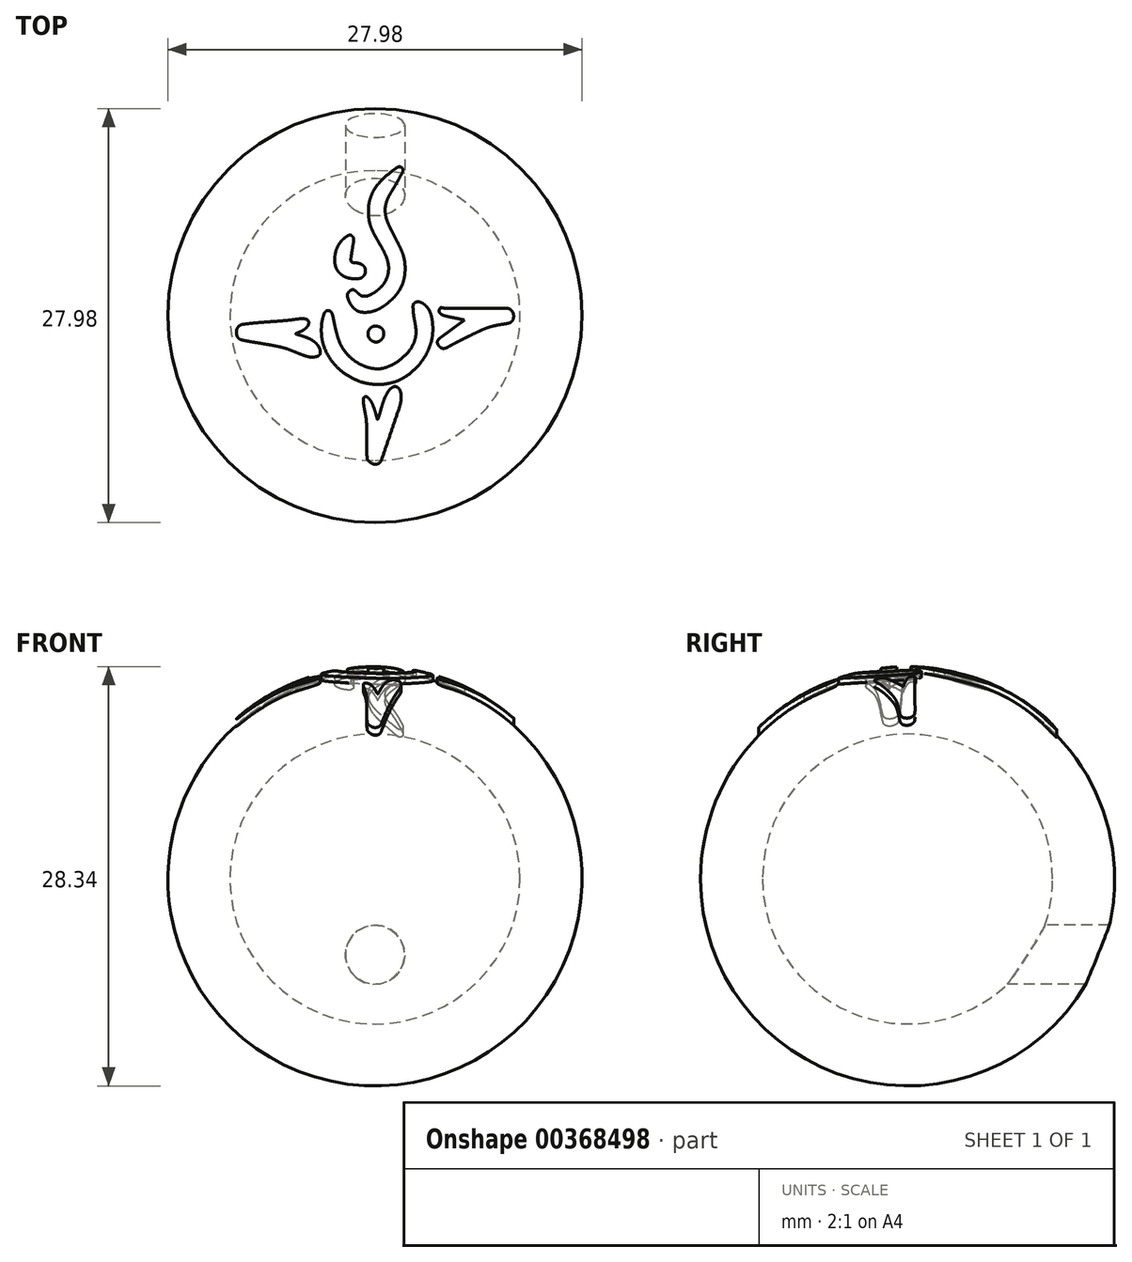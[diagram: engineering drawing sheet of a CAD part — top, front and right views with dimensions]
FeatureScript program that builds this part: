
annotation { "Feature Type Name" : "Feature", "Feature Type Description" : "" }
export const myFeature = defineFeature(function(context is Context, id is Id, definition is map)
    precondition{}
    {
        {
            var Q0;
            Q0=qCreatedBy(makeId("Top.planeOp"),FACE);
            var sketch = newSketch(context, id + "F0", { "sketchPlane" : qUnion([Q0])});
            skLineSegment(sketch, "E0", {"start": v(0, -10) * mm, "end": v(0, 10) * mm});
            skArc(sketch, "E1", {"start": v(0, 10) * mm, "mid": v(-10, 0) * mm, "end": v(0, -10) * mm});
            skSolve(sketch);
        }
        {
            var Q0;
            {var subQ0=sQuery(id+"F0.wireOp",EDGE,"E1");Q0=makeQuery(id+"F0.imprint","IMPRINT",FACE,{"disambiguationData":[TD([[makeQuery(id+"F0.imprint","IMPRINT",EDGE,{"derivedFrom":subQ0}),1.0]])]});}
            var Q1;
            Q1=sQuery(id+"F0.wireOp",EDGE,"E0");
            revolve(context, id + "F1", {"entities" : qUnion([Q0]), "axis" : qUnion([Q1]), "revolveType" : RevolveType.FULL});
        }
        {
            var Q0;
            Q0=makeQuery(id+"F1.opRevolve","SWEPT_BODY",BODY,{"disambiguationData":[OSD([sQuery(id+"F0.wireOp",EDGE,"E0"),sQuery(id+"F0.wireOp",EDGE,"E1")])]});
            var Q1;
            Q1=sQuery(id+"F0.wireOp",VERTEX,"NPe4G0ez-t7S9-9isL-QO5v-uuJu600mHcIT.center");
            var Q2;
            Q2=sQuery(id+"F0.wireOp",VERTEX,"E1.center");
            transform(context, id + "F2", {"entities" : qUnion([Q0]), "transformType" : TransformType.SCALE_UNIFORMLY, "scale" : 33.3, "scalePoint" : qUnion([Q2]), "makeCopy" : false});
        }
        {
            var Q0;
            Q0=qCreatedBy(makeId("Top.planeOp"),FACE);
            var sketch = newSketch(context, id + "F3", { "sketchPlane" : qUnion([Q0])});
            skArc(sketch, "E2", {"start": v(29.01, 233.55) * mm, "mid": v(19.13, 225.53) * mm, "end": v(9.84, 216.83) * mm});
            skArc(sketch, "E3", {"start": v(9.84, 216.83) * mm, "mid": v(3.12, 209.1) * mm, "end": v(-2.51, 200.54) * mm});
            skArc(sketch, "E4", {"start": v(-2.51, 200.54) * mm, "mid": v(-6.44, 192.13) * mm, "end": v(-9.04, 183.21) * mm});
            skArc(sketch, "E5", {"start": v(-9.04, 183.21) * mm, "mid": v(-10.44, 173.41) * mm, "end": v(-10.58, 163.51) * mm});
            skArc(sketch, "E6", {"start": v(-10.58, 163.51) * mm, "mid": v(-10.1, 157.75) * mm, "end": v(-9.24, 152.03) * mm});
            skArc(sketch, "E7", {"start": v(-9.24, 152.03) * mm, "mid": v(-8.07, 147.04) * mm, "end": v(-6.42, 142.18) * mm});
            skArc(sketch, "E8", {"start": v(-6.42, 142.18) * mm, "mid": v(-3.83, 136.15) * mm, "end": v(-0.88, 130.3) * mm});
            skArc(sketch, "E9", {"start": v(-0.88, 130.3) * mm, "mid": v(4.67, 120.25) * mm, "end": v(10.35, 110.28) * mm});
            skArc(sketch, "E10", {"start": v(10.35, 110.28) * mm, "mid": v(14.5, 102.5) * mm, "end": v(18.1, 94.45) * mm});
            skArc(sketch, "E11", {"start": v(18.1, 94.45) * mm, "mid": v(20.33, 87.78) * mm, "end": v(21.65, 80.87) * mm});
            skArc(sketch, "E12", {"start": v(21.65, 80.87) * mm, "mid": v(21.93, 74.62) * mm, "end": v(21.23, 68.4) * mm});
            skArc(sketch, "E13", {"start": v(21.23, 68.4) * mm, "mid": v(19.56, 62.07) * mm, "end": v(17.04, 56.03) * mm});
            skArc(sketch, "E14", {"start": v(17.04, 56.03) * mm, "mid": v(14.27, 51.34) * mm, "end": v(10.87, 47.1) * mm});
            skArc(sketch, "E15", {"start": v(10.87, 47.1) * mm, "mid": v(6.45, 42.75) * mm, "end": v(1.63, 38.84) * mm});
            skArc(sketch, "E16", {"start": v(1.63, 38.84) * mm, "mid": v(-3.27, 35.59) * mm, "end": v(-8.46, 32.84) * mm});
            skArc(sketch, "E17", {"start": v(-8.46, 32.84) * mm, "mid": v(-12.69, 31.4) * mm, "end": v(-17.12, 30.9) * mm});
            skArc(sketch, "E18", {"start": v(-17.12, 30.9) * mm, "mid": v(-18.57, 30.96) * mm, "end": v(-20.02, 31.11) * mm});
            skArc(sketch, "E19", {"start": v(-20.02, 31.11) * mm, "mid": v(-21.08, 31.35) * mm, "end": v(-22.08, 31.77) * mm});
            skArc(sketch, "E20", {"start": v(-22.08, 31.77) * mm, "mid": v(-23.2, 32.43) * mm, "end": v(-24.25, 33.22) * mm});
            skArc(sketch, "E21", {"start": v(-24.25, 33.22) * mm, "mid": v(-26.12, 34.84) * mm, "end": v(-27.96, 36.5) * mm});
            skArc(sketch, "E22", {"start": v(-27.96, 36.5) * mm, "mid": v(-29.65, 38.02) * mm, "end": v(-31.37, 39.52) * mm});
            skArc(sketch, "E23", {"start": v(-31.37, 39.52) * mm, "mid": v(-32.36, 40.29) * mm, "end": v(-33.42, 40.95) * mm});
            skArc(sketch, "E24", {"start": v(-33.42, 40.95) * mm, "mid": v(-34.2, 41.3) * mm, "end": v(-35.03, 41.5) * mm});
            skArc(sketch, "E25", {"start": v(-35.03, 41.5) * mm, "mid": v(-35.87, 41.54) * mm, "end": v(-36.7, 41.42) * mm});
            skArc(sketch, "E26", {"start": v(-36.7, 41.42) * mm, "mid": v(-38, 41) * mm, "end": v(-39.22, 40.4) * mm});
            skArc(sketch, "E27", {"start": v(-39.22, 40.4) * mm, "mid": v(-40.42, 39.6) * mm, "end": v(-41.52, 38.67) * mm});
            skArc(sketch, "E28", {"start": v(-41.52, 38.67) * mm, "mid": v(-42.45, 37.64) * mm, "end": v(-43.25, 36.51) * mm});
            skArc(sketch, "E29", {"start": v(-43.25, 36.51) * mm, "mid": v(-43.8, 35.42) * mm, "end": v(-44.14, 34.24) * mm});
            skArc(sketch, "E30", {"start": v(-44.14, 34.24) * mm, "mid": v(-44.33, 31.9) * mm, "end": v(-44.03, 29.59) * mm});
            skArc(sketch, "E31", {"start": v(-44.03, 29.59) * mm, "mid": v(-43.16, 26.53) * mm, "end": v(-42.02, 23.57) * mm});
            skArc(sketch, "E32", {"start": v(-42.02, 23.57) * mm, "mid": v(-40.5, 20.42) * mm, "end": v(-38.71, 17.4) * mm});
            skArc(sketch, "E33", {"start": v(-38.71, 17.4) * mm, "mid": v(-36.76, 14.69) * mm, "end": v(-34.56, 12.17) * mm});
            skArc(sketch, "E34", {"start": v(-34.56, 12.17) * mm, "mid": v(-32.5, 10.26) * mm, "end": v(-30.24, 8.58) * mm});
            skArc(sketch, "E35", {"start": v(-30.24, 8.58) * mm, "mid": v(-27.94, 7.28) * mm, "end": v(-25.49, 6.3) * mm});
            skArc(sketch, "E36", {"start": v(-25.49, 6.3) * mm, "mid": v(-22.72, 5.57) * mm, "end": v(-19.9, 5.18) * mm});
            skArc(sketch, "E37", {"start": v(-19.9, 5.18) * mm, "mid": v(-16.44, 5.03) * mm, "end": v(-12.99, 5.12) * mm});
            skArc(sketch, "E38", {"start": v(-12.99, 5.12) * mm, "mid": v(-7.73, 5.76) * mm, "end": v(-2.58, 7.01) * mm});
            skArc(sketch, "E39", {"start": v(-2.58, 7.01) * mm, "mid": v(2.77, 8.95) * mm, "end": v(7.9, 11.39) * mm});
            skArc(sketch, "E40", {"start": v(7.9, 11.39) * mm, "mid": v(13.3, 14.6) * mm, "end": v(18.4, 18.25) * mm});
            skArc(sketch, "E41", {"start": v(18.4, 18.25) * mm, "mid": v(23.75, 22.74) * mm, "end": v(28.83, 27.56) * mm});
            skArc(sketch, "E42", {"start": v(28.83, 27.56) * mm, "mid": v(33.48, 32.7) * mm, "end": v(37.66, 38.24) * mm});
            skArc(sketch, "E43", {"start": v(37.66, 38.24) * mm, "mid": v(41.04, 43.77) * mm, "end": v(43.8, 49.62) * mm});
            skArc(sketch, "E44", {"start": v(43.8, 49.62) * mm, "mid": v(45.9, 55.75) * mm, "end": v(47.34, 62.07) * mm});
            skArc(sketch, "E45", {"start": v(47.34, 62.07) * mm, "mid": v(48.2, 68.96) * mm, "end": v(48.46, 75.9) * mm});
            skArc(sketch, "E46", {"start": v(48.46, 75.9) * mm, "mid": v(48.28, 80.88) * mm, "end": v(47.83, 85.83) * mm});
            skArc(sketch, "E47", {"start": v(47.83, 85.83) * mm, "mid": v(47.14, 90.3) * mm, "end": v(46.11, 94.69) * mm});
            skArc(sketch, "E48", {"start": v(46.11, 94.69) * mm, "mid": v(44.7, 99.28) * mm, "end": v(42.96, 103.76) * mm});
            skArc(sketch, "E49", {"start": v(42.96, 103.76) * mm, "mid": v(40.56, 109.13) * mm, "end": v(37.96, 114.4) * mm});
            skArc(sketch, "E50", {"start": v(37.96, 114.4) * mm, "mid": v(32.65, 124.74) * mm, "end": v(27.37, 135.1) * mm});
            skArc(sketch, "E51", {"start": v(27.37, 135.1) * mm, "mid": v(24.73, 140.42) * mm, "end": v(22.2, 145.8) * mm});
            skArc(sketch, "E52", {"start": v(22.2, 145.8) * mm, "mid": v(20.66, 149.32) * mm, "end": v(19.27, 152.9) * mm});
            skArc(sketch, "E53", {"start": v(19.27, 152.9) * mm, "mid": v(18.3, 155.87) * mm, "end": v(17.54, 158.9) * mm});
            skArc(sketch, "E54", {"start": v(17.54, 158.9) * mm, "mid": v(16.72, 163.9) * mm, "end": v(16.36, 168.93) * mm});
            skArc(sketch, "E55", {"start": v(16.36, 168.93) * mm, "mid": v(16.52, 173.6) * mm, "end": v(17.22, 178.24) * mm});
            skArc(sketch, "E56", {"start": v(17.22, 178.24) * mm, "mid": v(18.5, 183.02) * mm, "end": v(20.27, 187.63) * mm});
            skArc(sketch, "E57", {"start": v(20.27, 187.63) * mm, "mid": v(22.83, 192.87) * mm, "end": v(25.73, 197.93) * mm});
            skArc(sketch, "E58", {"start": v(25.73, 197.93) * mm, "mid": v(28.95, 203.25) * mm, "end": v(32.1, 208.61) * mm});
            skArc(sketch, "E59", {"start": v(32.1, 208.61) * mm, "mid": v(35.38, 214.4) * mm, "end": v(38.59, 220.22) * mm});
            skArc(sketch, "E60", {"start": v(38.59, 220.22) * mm, "mid": v(41.58, 225.77) * mm, "end": v(44.55, 231.33) * mm});
            skArc(sketch, "E61", {"start": v(44.55, 231.33) * mm, "mid": v(45, 232.47) * mm, "end": v(45.14, 233.69) * mm});
            skArc(sketch, "E62", {"start": v(45.14, 233.69) * mm, "mid": v(45.05, 234.64) * mm, "end": v(44.77, 235.56) * mm});
            skArc(sketch, "E63", {"start": v(44.77, 235.56) * mm, "mid": v(44.32, 236.46) * mm, "end": v(43.72, 237.27) * mm});
            skArc(sketch, "E64", {"start": v(43.72, 237.27) * mm, "mid": v(42.97, 238) * mm, "end": v(42.1, 238.6) * mm});
            skArc(sketch, "E65", {"start": v(42.1, 238.6) * mm, "mid": v(41.14, 239.08) * mm, "end": v(40.11, 239.4) * mm});
            skArc(sketch, "E66", {"start": v(40.11, 239.4) * mm, "mid": v(39.26, 239.5) * mm, "end": v(38.42, 239.4) * mm});
            skArc(sketch, "E67", {"start": v(38.42, 239.4) * mm, "mid": v(37.38, 239.07) * mm, "end": v(36.4, 238.62) * mm});
            skArc(sketch, "E68", {"start": v(36.4, 238.62) * mm, "mid": v(34.96, 237.8) * mm, "end": v(33.58, 236.9) * mm});
            skArc(sketch, "E69", {"start": v(33.58, 236.9) * mm, "mid": v(31.29, 235.24) * mm, "end": v(29.01, 233.55) * mm});
            skArc(sketch, "E70", {"start": v(-45.92, 127.08) * mm, "mid": v(-50.13, 123.98) * mm, "end": v(-53.86, 120.31) * mm});
            skArc(sketch, "E71", {"start": v(-53.86, 120.31) * mm, "mid": v(-57.15, 116.09) * mm, "end": v(-59.87, 111.47) * mm});
            skArc(sketch, "E72", {"start": v(-59.87, 111.47) * mm, "mid": v(-62.06, 106.35) * mm, "end": v(-63.6, 101) * mm});
            skArc(sketch, "E73", {"start": v(-63.6, 101) * mm, "mid": v(-64.54, 95.27) * mm, "end": v(-64.85, 89.48) * mm});
            skArc(sketch, "E74", {"start": v(-64.85, 89.48) * mm, "mid": v(-64.72, 86.13) * mm, "end": v(-64.34, 82.8) * mm});
            skArc(sketch, "E75", {"start": v(-64.34, 82.8) * mm, "mid": v(-63.74, 79.95) * mm, "end": v(-62.82, 77.18) * mm});
            skArc(sketch, "E76", {"start": v(-62.82, 77.18) * mm, "mid": v(-61.64, 74.64) * mm, "end": v(-60.16, 72.26) * mm});
            skArc(sketch, "E77", {"start": v(-60.16, 72.26) * mm, "mid": v(-58.3, 69.89) * mm, "end": v(-56.23, 67.7) * mm});
            skArc(sketch, "E78", {"start": v(-56.23, 67.7) * mm, "mid": v(-54.01, 65.77) * mm, "end": v(-51.62, 64.06) * mm});
            skArc(sketch, "E79", {"start": v(-51.62, 64.06) * mm, "mid": v(-49.17, 62.64) * mm, "end": v(-46.6, 61.5) * mm});
            skArc(sketch, "E80", {"start": v(-46.6, 61.5) * mm, "mid": v(-43.73, 60.56) * mm, "end": v(-40.8, 59.9) * mm});
            skArc(sketch, "E81", {"start": v(-40.8, 59.9) * mm, "mid": v(-37.34, 59.42) * mm, "end": v(-33.86, 59.16) * mm});
            skArc(sketch, "E82", {"start": v(-33.86, 59.16) * mm, "mid": v(-30.5, 59.1) * mm, "end": v(-27.13, 59.26) * mm});
            skArc(sketch, "E83", {"start": v(-27.13, 59.26) * mm, "mid": v(-24.75, 59.62) * mm, "end": v(-22.46, 60.36) * mm});
            skArc(sketch, "E84", {"start": v(-22.46, 60.36) * mm, "mid": v(-20.66, 61.32) * mm, "end": v(-19.1, 62.63) * mm});
            skArc(sketch, "E85", {"start": v(-19.1, 62.63) * mm, "mid": v(-17.66, 64.36) * mm, "end": v(-16.5, 66.28) * mm});
            skArc(sketch, "E86", {"start": v(-16.5, 66.28) * mm, "mid": v(-15.4, 69.6) * mm, "end": v(-15.24, 73.08) * mm});
            skArc(sketch, "E87", {"start": v(-15.24, 73.08) * mm, "mid": v(-16.08, 76.33) * mm, "end": v(-17.88, 79.16) * mm});
            skArc(sketch, "E88", {"start": v(-17.88, 79.16) * mm, "mid": v(-20.75, 81.68) * mm, "end": v(-24.17, 83.38) * mm});
            skArc(sketch, "E89", {"start": v(-24.17, 83.38) * mm, "mid": v(-28.48, 84.49) * mm, "end": v(-32.91, 84.88) * mm});
            skArc(sketch, "E90", {"start": v(-32.91, 84.88) * mm, "mid": v(-34.86, 85.1) * mm, "end": v(-36.73, 85.7) * mm});
            skArc(sketch, "E91", {"start": v(-36.73, 85.7) * mm, "mid": v(-37.9, 86.6) * mm, "end": v(-38.52, 87.91) * mm});
            skArc(sketch, "E92", {"start": v(-38.52, 87.91) * mm, "mid": v(-38.8, 90.23) * mm, "end": v(-38.7, 92.56) * mm});
            skArc(sketch, "E93", {"start": v(-38.7, 92.56) * mm, "mid": v(-37.86, 98.3) * mm, "end": v(-36.95, 104.03) * mm});
            skArc(sketch, "E94", {"start": v(-36.95, 104.03) * mm, "mid": v(-35.78, 111.04) * mm, "end": v(-34.64, 118.06) * mm});
            skArc(sketch, "E95", {"start": v(-34.64, 118.06) * mm, "mid": v(-34.36, 120.3) * mm, "end": v(-34.22, 122.54) * mm});
            skArc(sketch, "E96", {"start": v(-34.22, 122.54) * mm, "mid": v(-34.32, 123.85) * mm, "end": v(-34.7, 125.11) * mm});
            skArc(sketch, "E97", {"start": v(-34.7, 125.11) * mm, "mid": v(-35.37, 126.33) * mm, "end": v(-36.26, 127.4) * mm});
            skArc(sketch, "E98", {"start": v(-36.26, 127.4) * mm, "mid": v(-37.31, 128.36) * mm, "end": v(-38.46, 129.21) * mm});
            skArc(sketch, "E99", {"start": v(-38.46, 129.21) * mm, "mid": v(-39.3, 129.61) * mm, "end": v(-40.24, 129.73) * mm});
            skArc(sketch, "E100", {"start": v(-40.24, 129.73) * mm, "mid": v(-41.31, 129.57) * mm, "end": v(-42.32, 129.17) * mm});
            skArc(sketch, "E101", {"start": v(-42.32, 129.17) * mm, "mid": v(-44.14, 128.16) * mm, "end": v(-45.92, 127.08) * mm});
            skArc(sketch, "E102", {"start": v(65.46, 21.4) * mm, "mid": v(64.85, 21.12) * mm, "end": v(64.26, 20.79) * mm});
            skArc(sketch, "E103", {"start": v(64.26, 20.79) * mm, "mid": v(63.68, 20.42) * mm, "end": v(63.13, 20) * mm});
            skArc(sketch, "E104", {"start": v(63.13, 20) * mm, "mid": v(62.68, 19.6) * mm, "end": v(62.25, 19.18) * mm});
            skArc(sketch, "E105", {"start": v(62.25, 19.18) * mm, "mid": v(61.98, 18.83) * mm, "end": v(61.79, 18.44) * mm});
            skArc(sketch, "E106", {"start": v(61.79, 18.44) * mm, "mid": v(61.29, 16.67) * mm, "end": v(61.1, 14.84) * mm});
            skArc(sketch, "E107", {"start": v(61.1, 14.84) * mm, "mid": v(61.15, 11.63) * mm, "end": v(61.3, 8.43) * mm});
            skArc(sketch, "E108", {"start": v(61.3, 8.43) * mm, "mid": v(61.65, 4.5) * mm, "end": v(62.14, 0.6) * mm});
            skArc(sketch, "E109", {"start": v(62.14, 0.6) * mm, "mid": v(62.82, -3.76) * mm, "end": v(63.62, -8.1) * mm});
            skArc(sketch, "E110", {"start": v(63.62, -8.1) * mm, "mid": v(64.53, -12.99) * mm, "end": v(65.32, -17.9) * mm});
            skArc(sketch, "E111", {"start": v(65.32, -17.9) * mm, "mid": v(65.76, -21.56) * mm, "end": v(65.99, -25.23) * mm});
            skArc(sketch, "E112", {"start": v(65.99, -25.23) * mm, "mid": v(65.98, -28.33) * mm, "end": v(65.74, -31.42) * mm});
            skArc(sketch, "E113", {"start": v(65.74, -31.42) * mm, "mid": v(65.29, -34.5) * mm, "end": v(64.6, -37.55) * mm});
            skArc(sketch, "E114", {"start": v(64.6, -37.55) * mm, "mid": v(61.01, -47.26) * mm, "end": v(55.57, -56.05) * mm});
            skArc(sketch, "E115", {"start": v(55.57, -56.05) * mm, "mid": v(47.83, -64.8) * mm, "end": v(38.95, -72.38) * mm});
            skArc(sketch, "E116", {"start": v(38.95, -72.38) * mm, "mid": v(29.3, -78.52) * mm, "end": v(18.86, -83.23) * mm});
            skArc(sketch, "E117", {"start": v(18.86, -83.23) * mm, "mid": v(9.39, -85.53) * mm, "end": v(-0.36, -85.64) * mm});
            skArc(sketch, "E118", {"start": v(-0.36, -85.64) * mm, "mid": v(-9.01, -84.12) * mm, "end": v(-17.37, -81.43) * mm});
            skArc(sketch, "E119", {"start": v(-17.37, -81.43) * mm, "mid": v(-25.6, -77.52) * mm, "end": v(-33.3, -72.63) * mm});
            skArc(sketch, "E120", {"start": v(-33.3, -72.63) * mm, "mid": v(-40.35, -66.8) * mm, "end": v(-46.63, -60.13) * mm});
            skArc(sketch, "E121", {"start": v(-46.63, -60.13) * mm, "mid": v(-51.86, -52.93) * mm, "end": v(-56.07, -45.1) * mm});
            skArc(sketch, "E122", {"start": v(-56.07, -45.1) * mm, "mid": v(-57.45, -41.85) * mm, "end": v(-58.65, -38.55) * mm});
            skArc(sketch, "E123", {"start": v(-58.65, -38.55) * mm, "mid": v(-59.98, -34.42) * mm, "end": v(-61.19, -30.25) * mm});
            skArc(sketch, "E124", {"start": v(-61.19, -30.25) * mm, "mid": v(-62.51, -25.22) * mm, "end": v(-63.72, -20.17) * mm});
            skArc(sketch, "E125", {"start": v(-63.72, -20.17) * mm, "mid": v(-65.05, -14.14) * mm, "end": v(-66.29, -8.1) * mm});
            skArc(sketch, "E126", {"start": v(-66.29, -8.1) * mm, "mid": v(-67.21, -3.72) * mm, "end": v(-68.25, 0.62) * mm});
            skArc(sketch, "E127", {"start": v(-68.25, 0.62) * mm, "mid": v(-68.99, 2.87) * mm, "end": v(-70.04, 4.98) * mm});
            skArc(sketch, "E128", {"start": v(-70.04, 4.98) * mm, "mid": v(-71.06, 6.23) * mm, "end": v(-72.4, 7.13) * mm});
            skArc(sketch, "E129", {"start": v(-72.4, 7.13) * mm, "mid": v(-74.06, 7.7) * mm, "end": v(-75.82, 7.9) * mm});
            skArc(sketch, "E130", {"start": v(-75.82, 7.9) * mm, "mid": v(-77.16, 7.74) * mm, "end": v(-78.43, 7.27) * mm});
            skArc(sketch, "E131", {"start": v(-78.43, 7.27) * mm, "mid": v(-79.54, 6.5) * mm, "end": v(-80.43, 5.5) * mm});
            skArc(sketch, "E132", {"start": v(-80.43, 5.5) * mm, "mid": v(-81.4, 3.84) * mm, "end": v(-82.13, 2.07) * mm});
            skArc(sketch, "E133", {"start": v(-82.13, 2.07) * mm, "mid": v(-83.1, -1) * mm, "end": v(-83.99, -4.1) * mm});
            skArc(sketch, "E134", {"start": v(-83.99, -4.1) * mm, "mid": v(-85.1, -9.01) * mm, "end": v(-85.83, -14) * mm});
            skArc(sketch, "E135", {"start": v(-85.83, -14) * mm, "mid": v(-86.25, -19.46) * mm, "end": v(-86.34, -24.93) * mm});
            skArc(sketch, "E136", {"start": v(-86.34, -24.93) * mm, "mid": v(-86.1, -30.38) * mm, "end": v(-85.54, -35.8) * mm});
            skArc(sketch, "E137", {"start": v(-85.54, -35.8) * mm, "mid": v(-84.67, -40.74) * mm, "end": v(-83.43, -45.6) * mm});
            skArc(sketch, "E138", {"start": v(-83.43, -45.6) * mm, "mid": v(-77.13, -61.14) * mm, "end": v(-68, -75.2) * mm});
            skArc(sketch, "E139", {"start": v(-68, -75.2) * mm, "mid": v(-56.22, -87.58) * mm, "end": v(-42.42, -97.64) * mm});
            skArc(sketch, "E140", {"start": v(-42.42, -97.64) * mm, "mid": v(-27.05, -105.06) * mm, "end": v(-10.6, -109.6) * mm});
            skArc(sketch, "E141", {"start": v(-10.6, -109.6) * mm, "mid": v(6.07, -111) * mm, "end": v(22.7, -109.2) * mm});
            skArc(sketch, "E142", {"start": v(22.7, -109.2) * mm, "mid": v(34.18, -105.87) * mm, "end": v(45, -100.8) * mm});
            skArc(sketch, "E143", {"start": v(45, -100.8) * mm, "mid": v(55.53, -93.83) * mm, "end": v(65.05, -85.53) * mm});
            skArc(sketch, "E144", {"start": v(65.05, -85.53) * mm, "mid": v(73.6, -75.81) * mm, "end": v(80.84, -65.07) * mm});
            skArc(sketch, "E145", {"start": v(80.84, -65.07) * mm, "mid": v(86.55, -53.59) * mm, "end": v(90.67, -41.45) * mm});
            skArc(sketch, "E146", {"start": v(90.67, -41.45) * mm, "mid": v(91.87, -36) * mm, "end": v(92.6, -30.49) * mm});
            skArc(sketch, "E147", {"start": v(92.6, -30.49) * mm, "mid": v(92.96, -24.25) * mm, "end": v(92.94, -18) * mm});
            skArc(sketch, "E148", {"start": v(92.94, -18) * mm, "mid": v(92.53, -11.87) * mm, "end": v(91.75, -5.78) * mm});
            skArc(sketch, "E149", {"start": v(91.75, -5.78) * mm, "mid": v(90.67, -0.67) * mm, "end": v(89.09, 4.31) * mm});
            skArc(sketch, "E150", {"start": v(89.09, 4.31) * mm, "mid": v(87.2, 8.44) * mm, "end": v(84.75, 12.25) * mm});
            skArc(sketch, "E151", {"start": v(84.75, 12.25) * mm, "mid": v(81.83, 15.6) * mm, "end": v(78.44, 18.46) * mm});
            skArc(sketch, "E152", {"start": v(78.44, 18.46) * mm, "mid": v(75.14, 20.43) * mm, "end": v(71.54, 21.78) * mm});
            skArc(sketch, "E153", {"start": v(71.54, 21.78) * mm, "mid": v(68.47, 22.1) * mm, "end": v(65.46, 21.4) * mm});
            skArc(sketch, "E154", {"start": v(103.85, 10.27) * mm, "mid": v(103.2, 8.18) * mm, "end": v(103.3, 5.98) * mm});
            skArc(sketch, "E155", {"start": v(103.3, 5.98) * mm, "mid": v(104.13, 4.02) * mm, "end": v(105.62, 2.5) * mm});
            skArc(sketch, "E156", {"start": v(105.62, 2.5) * mm, "mid": v(108.58, 0.82) * mm, "end": v(111.77, -0.35) * mm});
            skArc(sketch, "E157", {"start": v(111.77, -0.35) * mm, "mid": v(117.43, -1.78) * mm, "end": v(123.14, -3) * mm});
            skArc(sketch, "E158", {"start": v(123.14, -3) * mm, "mid": v(125.34, -3.44) * mm, "end": v(127.55, -3.88) * mm});
            skArc(sketch, "E159", {"start": v(127.55, -3.88) * mm, "mid": v(129.83, -4.33) * mm, "end": v(132.11, -4.78) * mm});
            skArc(sketch, "E160", {"start": v(132.11, -4.78) * mm, "mid": v(134.16, -5.19) * mm, "end": v(136.2, -5.6) * mm});
            skArc(sketch, "E161", {"start": v(136.2, -5.6) * mm, "mid": v(137.57, -5.88) * mm, "end": v(138.94, -6.16) * mm});
            skLineSegment(sketch, "E162", {"start": v(138.94, -6.16) * mm, "end": v(144.24, -7.26) * mm});
            skLineSegment(sketch, "E163", {"start": v(144.24, -7.26) * mm, "end": v(138.6, -11.21) * mm});
            skArc(sketch, "E164", {"start": v(138.6, -11.21) * mm, "mid": v(137.18, -12.21) * mm, "end": v(135.77, -13.23) * mm});
            skArc(sketch, "E165", {"start": v(135.77, -13.23) * mm, "mid": v(133.77, -14.68) * mm, "end": v(131.77, -16.14) * mm});
            skArc(sketch, "E166", {"start": v(131.77, -16.14) * mm, "mid": v(129.58, -17.75) * mm, "end": v(127.4, -19.37) * mm});
            skArc(sketch, "E167", {"start": v(127.4, -19.37) * mm, "mid": v(125.35, -20.9) * mm, "end": v(123.3, -22.45) * mm});
            skArc(sketch, "E168", {"start": v(123.3, -22.45) * mm, "mid": v(121.22, -24) * mm, "end": v(119.15, -25.54) * mm});
            skArc(sketch, "E169", {"start": v(119.15, -25.54) * mm, "mid": v(116.91, -27.18) * mm, "end": v(114.67, -28.8) * mm});
            skArc(sketch, "E170", {"start": v(114.67, -28.8) * mm, "mid": v(112.6, -30.3) * mm, "end": v(110.53, -31.78) * mm});
            skArc(sketch, "E171", {"start": v(110.53, -31.78) * mm, "mid": v(109.02, -32.83) * mm, "end": v(107.5, -33.87) * mm});
            skArc(sketch, "E172", {"start": v(107.5, -33.87) * mm, "mid": v(104.91, -35.81) * mm, "end": v(102.52, -38) * mm});
            skArc(sketch, "E173", {"start": v(102.52, -38) * mm, "mid": v(101.18, -39.8) * mm, "end": v(100.4, -41.9) * mm});
            skArc(sketch, "E174", {"start": v(100.4, -41.9) * mm, "mid": v(100.3, -43.94) * mm, "end": v(100.88, -45.9) * mm});
            skArc(sketch, "E175", {"start": v(100.88, -45.9) * mm, "mid": v(102.25, -48.24) * mm, "end": v(103.94, -50.34) * mm});
            skArc(sketch, "E176", {"start": v(103.94, -50.34) * mm, "mid": v(105.3, -51.53) * mm, "end": v(106.85, -52.43) * mm});
            skArc(sketch, "E177", {"start": v(106.85, -52.43) * mm, "mid": v(108.5, -52.96) * mm, "end": v(110.22, -53.1) * mm});
            skArc(sketch, "E178", {"start": v(110.22, -53.1) * mm, "mid": v(112.2, -52.89) * mm, "end": v(114.12, -52.31) * mm});
            skArc(sketch, "E179", {"start": v(114.12, -52.31) * mm, "mid": v(116.4, -51.27) * mm, "end": v(118.59, -50.02) * mm});
            skArc(sketch, "E180", {"start": v(118.59, -50.02) * mm, "mid": v(120.15, -49.08) * mm, "end": v(121.76, -48.19) * mm});
            skArc(sketch, "E181", {"start": v(121.76, -48.19) * mm, "mid": v(125.82, -46.06) * mm, "end": v(129.89, -43.95) * mm});
            skArc(sketch, "E182", {"start": v(129.89, -43.95) * mm, "mid": v(134.76, -41.44) * mm, "end": v(139.64, -38.96) * mm});
            skArc(sketch, "E183", {"start": v(139.64, -38.96) * mm, "mid": v(144.95, -36.29) * mm, "end": v(150.27, -33.64) * mm});
            skArc(sketch, "E184", {"start": v(150.27, -33.64) * mm, "mid": v(159.77, -29) * mm, "end": v(169.33, -24.46) * mm});
            skArc(sketch, "E185", {"start": v(169.33, -24.46) * mm, "mid": v(175.2, -21.89) * mm, "end": v(181.2, -19.6) * mm});
            skArc(sketch, "E186", {"start": v(181.2, -19.6) * mm, "mid": v(186.48, -17.91) * mm, "end": v(191.84, -16.56) * mm});
            skArc(sketch, "E187", {"start": v(191.84, -16.56) * mm, "mid": v(198.67, -15.2) * mm, "end": v(205.54, -14.04) * mm});
            skArc(sketch, "E188", {"start": v(205.54, -14.04) * mm, "mid": v(208.79, -13.53) * mm, "end": v(212.03, -12.98) * mm});
            skArc(sketch, "E189", {"start": v(212.03, -12.98) * mm, "mid": v(213.87, -12.6) * mm, "end": v(215.7, -12.11) * mm});
            skArc(sketch, "E190", {"start": v(215.7, -12.11) * mm, "mid": v(216.92, -11.68) * mm, "end": v(218.09, -11.13) * mm});
            skArc(sketch, "E191", {"start": v(218.09, -11.13) * mm, "mid": v(219.06, -10.5) * mm, "end": v(219.93, -9.76) * mm});
            skArc(sketch, "E192", {"start": v(219.93, -9.76) * mm, "mid": v(221.11, -8.3) * mm, "end": v(221.97, -6.62) * mm});
            skArc(sketch, "E193", {"start": v(221.97, -6.62) * mm, "mid": v(222.6, -4.57) * mm, "end": v(222.93, -2.44) * mm});
            skArc(sketch, "E194", {"start": v(222.93, -2.44) * mm, "mid": v(222.96, -0.25) * mm, "end": v(222.7, 1.92) * mm});
            skArc(sketch, "E195", {"start": v(222.7, 1.92) * mm, "mid": v(222.14, 3.83) * mm, "end": v(221.24, 5.6) * mm});
            skArc(sketch, "E196", {"start": v(221.24, 5.6) * mm, "mid": v(219.73, 7.65) * mm, "end": v(217.92, 9.44) * mm});
            skArc(sketch, "E197", {"start": v(217.92, 9.44) * mm, "mid": v(216.13, 10.6) * mm, "end": v(214.1, 11.29) * mm});
            skArc(sketch, "E198", {"start": v(214.1, 11.29) * mm, "mid": v(210.86, 11.76) * mm, "end": v(207.59, 11.92) * mm});
            skArc(sketch, "E199", {"start": v(207.59, 11.92) * mm, "mid": v(198.73, 11.88) * mm, "end": v(189.88, 11.78) * mm});
            skArc(sketch, "E200", {"start": v(189.88, 11.78) * mm, "mid": v(175.63, 11.6) * mm, "end": v(161.38, 11.47) * mm});
            skArc(sketch, "E201", {"start": v(161.38, 11.47) * mm, "mid": v(148.64, 11.43) * mm, "end": v(135.9, 11.47) * mm});
            skArc(sketch, "E202", {"start": v(135.9, 11.47) * mm, "mid": v(125.01, 11.56) * mm, "end": v(114.12, 11.68) * mm});
            skArc(sketch, "E203", {"start": v(114.12, 11.68) * mm, "mid": v(111.53, 11.85) * mm, "end": v(108.98, 12.3) * mm});
            skArc(sketch, "E204", {"start": v(108.98, 12.3) * mm, "mid": v(107.88, 12.53) * mm, "end": v(106.78, 12.7) * mm});
            skArc(sketch, "E205", {"start": v(106.78, 12.7) * mm, "mid": v(106.2, 12.72) * mm, "end": v(105.65, 12.58) * mm});
            skArc(sketch, "E206", {"start": v(105.65, 12.58) * mm, "mid": v(105.18, 12.3) * mm, "end": v(104.81, 11.9) * mm});
            skArc(sketch, "E207", {"start": v(104.81, 11.9) * mm, "mid": v(104.3, 11.1) * mm, "end": v(103.85, 10.27) * mm});
            skArc(sketch, "E208", {"start": v(-131.36, -6.65) * mm, "mid": v(-133.6, -7) * mm, "end": v(-135.83, -7.27) * mm});
            skArc(sketch, "E209", {"start": v(-135.83, -7.27) * mm, "mid": v(-139.72, -7.68) * mm, "end": v(-143.62, -8.06) * mm});
            skArc(sketch, "E210", {"start": v(-143.62, -8.06) * mm, "mid": v(-148.14, -8.47) * mm, "end": v(-152.66, -8.86) * mm});
            skArc(sketch, "E211", {"start": v(-152.66, -8.86) * mm, "mid": v(-157.26, -9.22) * mm, "end": v(-161.86, -9.55) * mm});
            skArc(sketch, "E212", {"start": v(-161.86, -9.55) * mm, "mid": v(-173.2, -10.37) * mm, "end": v(-184.55, -11.25) * mm});
            skArc(sketch, "E213", {"start": v(-184.55, -11.25) * mm, "mid": v(-192.69, -11.96) * mm, "end": v(-200.81, -12.79) * mm});
            skArc(sketch, "E214", {"start": v(-200.81, -12.79) * mm, "mid": v(-206.72, -13.48) * mm, "end": v(-212.61, -14.24) * mm});
            skArc(sketch, "E215", {"start": v(-212.61, -14.24) * mm, "mid": v(-214.78, -14.73) * mm, "end": v(-216.83, -15.58) * mm});
            skArc(sketch, "E216", {"start": v(-216.83, -15.58) * mm, "mid": v(-219.48, -17.53) * mm, "end": v(-221.38, -20.22) * mm});
            skArc(sketch, "E217", {"start": v(-221.38, -20.22) * mm, "mid": v(-222.6, -23.66) * mm, "end": v(-222.98, -27.29) * mm});
            skArc(sketch, "E218", {"start": v(-222.98, -27.29) * mm, "mid": v(-222.51, -30.87) * mm, "end": v(-221.21, -34.25) * mm});
            skArc(sketch, "E219", {"start": v(-221.21, -34.25) * mm, "mid": v(-219.25, -36.82) * mm, "end": v(-216.57, -38.61) * mm});
            skArc(sketch, "E220", {"start": v(-216.57, -38.61) * mm, "mid": v(-215.48, -39.03) * mm, "end": v(-214.35, -39.34) * mm});
            skArc(sketch, "E221", {"start": v(-214.35, -39.34) * mm, "mid": v(-211.03, -40.03) * mm, "end": v(-207.7, -40.7) * mm});
            skArc(sketch, "E222", {"start": v(-207.7, -40.7) * mm, "mid": v(-203.7, -41.46) * mm, "end": v(-199.71, -42.18) * mm});
            skArc(sketch, "E223", {"start": v(-199.71, -42.18) * mm, "mid": v(-195.29, -42.94) * mm, "end": v(-190.86, -43.67) * mm});
            skArc(sketch, "E224", {"start": v(-190.86, -43.67) * mm, "mid": v(-179.98, -45.46) * mm, "end": v(-169.1, -47.31) * mm});
            skArc(sketch, "E225", {"start": v(-169.1, -47.31) * mm, "mid": v(-161.88, -48.66) * mm, "end": v(-154.68, -50.16) * mm});
            skArc(sketch, "E226", {"start": v(-154.68, -50.16) * mm, "mid": v(-149.45, -51.4) * mm, "end": v(-144.25, -52.8) * mm});
            skArc(sketch, "E227", {"start": v(-144.25, -52.8) * mm, "mid": v(-140.08, -54.14) * mm, "end": v(-135.99, -55.72) * mm});
            skArc(sketch, "E228", {"start": v(-135.99, -55.72) * mm, "mid": v(-130.47, -58) * mm, "end": v(-124.93, -60.26) * mm});
            skArc(sketch, "E229", {"start": v(-124.93, -60.26) * mm, "mid": v(-120.71, -61.9) * mm, "end": v(-116.47, -63.47) * mm});
            skArc(sketch, "E230", {"start": v(-116.47, -63.47) * mm, "mid": v(-113.25, -64.59) * mm, "end": v(-110, -65.63) * mm});
            skArc(sketch, "E231", {"start": v(-110, -65.63) * mm, "mid": v(-107.83, -66.2) * mm, "end": v(-105.61, -66.62) * mm});
            skArc(sketch, "E232", {"start": v(-105.61, -66.62) * mm, "mid": v(-103.25, -66.88) * mm, "end": v(-100.88, -66.95) * mm});
            skArc(sketch, "E233", {"start": v(-100.88, -66.95) * mm, "mid": v(-98.54, -66.85) * mm, "end": v(-96.2, -66.56) * mm});
            skArc(sketch, "E234", {"start": v(-96.2, -66.56) * mm, "mid": v(-94.2, -66.14) * mm, "end": v(-92.24, -65.56) * mm});
            skArc(sketch, "E235", {"start": v(-92.24, -65.56) * mm, "mid": v(-90.93, -64.93) * mm, "end": v(-89.79, -64.02) * mm});
            skArc(sketch, "E236", {"start": v(-89.79, -64.02) * mm, "mid": v(-88.55, -62.26) * mm, "end": v(-88, -60.17) * mm});
            skArc(sketch, "E237", {"start": v(-88, -60.17) * mm, "mid": v(-88.02, -57.48) * mm, "end": v(-88.54, -54.84) * mm});
            skArc(sketch, "E238", {"start": v(-88.54, -54.84) * mm, "mid": v(-89.66, -51.83) * mm, "end": v(-91.23, -49.03) * mm});
            skArc(sketch, "E239", {"start": v(-91.23, -49.03) * mm, "mid": v(-93.28, -46.32) * mm, "end": v(-95.66, -43.89) * mm});
            skArc(sketch, "E240", {"start": v(-95.66, -43.89) * mm, "mid": v(-97.72, -42.15) * mm, "end": v(-99.9, -40.55) * mm});
            skArc(sketch, "E241", {"start": v(-99.9, -40.55) * mm, "mid": v(-102.15, -39.12) * mm, "end": v(-104.5, -37.84) * mm});
            skArc(sketch, "E242", {"start": v(-104.5, -37.84) * mm, "mid": v(-107.34, -36.51) * mm, "end": v(-110.26, -35.34) * mm});
            skArc(sketch, "E243", {"start": v(-110.26, -35.34) * mm, "mid": v(-114.24, -33.92) * mm, "end": v(-118.25, -32.59) * mm});
            skLineSegment(sketch, "E244", {"start": v(-118.25, -32.59) * mm, "end": v(-128.14, -29.44) * mm});
            skLineSegment(sketch, "E245", {"start": v(-128.14, -29.44) * mm, "end": v(-122.48, -27.14) * mm});
            skArc(sketch, "E246", {"start": v(-122.48, -27.14) * mm, "mid": v(-119.78, -25.96) * mm, "end": v(-117.15, -24.64) * mm});
            skArc(sketch, "E247", {"start": v(-117.15, -24.64) * mm, "mid": v(-114.93, -23.33) * mm, "end": v(-112.83, -21.85) * mm});
            skArc(sketch, "E248", {"start": v(-112.83, -21.85) * mm, "mid": v(-111.13, -20.42) * mm, "end": v(-109.57, -18.83) * mm});
            skArc(sketch, "E249", {"start": v(-109.57, -18.83) * mm, "mid": v(-108.4, -17.3) * mm, "end": v(-107.44, -15.62) * mm});
            skArc(sketch, "E250", {"start": v(-107.44, -15.62) * mm, "mid": v(-106.65, -12.83) * mm, "end": v(-106.8, -9.93) * mm});
            skArc(sketch, "E251", {"start": v(-106.8, -9.93) * mm, "mid": v(-107.92, -7.7) * mm, "end": v(-109.97, -6.27) * mm});
            skArc(sketch, "E252", {"start": v(-109.97, -6.27) * mm, "mid": v(-113.9, -5.25) * mm, "end": v(-117.95, -5.09) * mm});
            skArc(sketch, "E253", {"start": v(-117.95, -5.09) * mm, "mid": v(-124.68, -5.7) * mm, "end": v(-131.36, -6.65) * mm});
            skArc(sketch, "E254", {"start": v(-6.77, -19.67) * mm, "mid": v(-9.2, -22.4) * mm, "end": v(-10.77, -25.7) * mm});
            skArc(sketch, "E255", {"start": v(-10.77, -25.7) * mm, "mid": v(-11.35, -29.33) * mm, "end": v(-10.89, -32.97) * mm});
            skArc(sketch, "E256", {"start": v(-10.89, -32.97) * mm, "mid": v(-9.42, -36.37) * mm, "end": v(-7.06, -39.22) * mm});
            skArc(sketch, "E257", {"start": v(-7.06, -39.22) * mm, "mid": v(-4, -41.32) * mm, "end": v(-0.49, -42.5) * mm});
            skArc(sketch, "E258", {"start": v(-0.49, -42.5) * mm, "mid": v(2.99, -42.62) * mm, "end": v(6.33, -41.7) * mm});
            skArc(sketch, "E259", {"start": v(6.33, -41.7) * mm, "mid": v(9.37, -39.8) * mm, "end": v(11.78, -37.15) * mm});
            skArc(sketch, "E260", {"start": v(11.78, -37.15) * mm, "mid": v(13.43, -33.86) * mm, "end": v(14.16, -30.26) * mm});
            skArc(sketch, "E261", {"start": v(14.16, -30.26) * mm, "mid": v(13.9, -26.62) * mm, "end": v(12.68, -23.18) * mm});
            skArc(sketch, "E262", {"start": v(12.68, -23.18) * mm, "mid": v(11.21, -21.09) * mm, "end": v(9.23, -19.47) * mm});
            skArc(sketch, "E263", {"start": v(9.23, -19.47) * mm, "mid": v(6.62, -18.2) * mm, "end": v(3.8, -17.4) * mm});
            skArc(sketch, "E264", {"start": v(3.8, -17.4) * mm, "mid": v(0.87, -17.15) * mm, "end": v(-2.06, -17.43) * mm});
            skArc(sketch, "E265", {"start": v(-2.06, -17.43) * mm, "mid": v(-4.56, -18.25) * mm, "end": v(-6.77, -19.67) * mm});
            skArc(sketch, "E266", {"start": v(27.49, -116.02) * mm, "mid": v(24.94, -117.92) * mm, "end": v(22.78, -120.24) * mm});
            skArc(sketch, "E267", {"start": v(22.78, -120.24) * mm, "mid": v(20.4, -123.6) * mm, "end": v(18.33, -127.14) * mm});
            skArc(sketch, "E268", {"start": v(18.33, -127.14) * mm, "mid": v(16.08, -131.78) * mm, "end": v(14.16, -136.56) * mm});
            skArc(sketch, "E269", {"start": v(14.16, -136.56) * mm, "mid": v(12.1, -142.55) * mm, "end": v(10.27, -148.62) * mm});
            skArc(sketch, "E270", {"start": v(10.27, -148.62) * mm, "mid": v(8.7, -154.13) * mm, "end": v(7.12, -159.63) * mm});
            skArc(sketch, "E271", {"start": v(7.12, -159.63) * mm, "mid": v(6.33, -162.23) * mm, "end": v(5.48, -164.8) * mm});
            skArc(sketch, "E272", {"start": v(5.48, -164.8) * mm, "mid": v(5.01, -166) * mm, "end": v(4.46, -167.15) * mm});
            skArc(sketch, "E273", {"start": v(4.46, -167.15) * mm, "mid": v(4.15, -167.32) * mm, "end": v(3.87, -167.1) * mm});
            skArc(sketch, "E274", {"start": v(3.87, -167.1) * mm, "mid": v(3.71, -166.6) * mm, "end": v(3.56, -166.1) * mm});
            skArc(sketch, "E275", {"start": v(3.56, -166.1) * mm, "mid": v(3.15, -164.68) * mm, "end": v(2.74, -163.27) * mm});
            skArc(sketch, "E276", {"start": v(2.74, -163.27) * mm, "mid": v(2.25, -161.58) * mm, "end": v(1.76, -159.89) * mm});
            skArc(sketch, "E277", {"start": v(1.76, -159.89) * mm, "mid": v(1.23, -158.03) * mm, "end": v(0.7, -156.17) * mm});
            skArc(sketch, "E278", {"start": v(0.7, -156.17) * mm, "mid": v(-1.17, -150.27) * mm, "end": v(-3.35, -144.48) * mm});
            skArc(sketch, "E279", {"start": v(-3.35, -144.48) * mm, "mid": v(-5.42, -140.1) * mm, "end": v(-7.98, -135.98) * mm});
            skArc(sketch, "E280", {"start": v(-7.98, -135.98) * mm, "mid": v(-10.1, -133.45) * mm, "end": v(-12.64, -131.33) * mm});
            skArc(sketch, "E281", {"start": v(-12.64, -131.33) * mm, "mid": v(-14.72, -130.62) * mm, "end": v(-16.86, -131.1) * mm});
            skArc(sketch, "E282", {"start": v(-16.86, -131.1) * mm, "mid": v(-17.88, -131.97) * mm, "end": v(-18.44, -133.2) * mm});
            skArc(sketch, "E283", {"start": v(-18.44, -133.2) * mm, "mid": v(-18.75, -135.34) * mm, "end": v(-18.81, -137.5) * mm});
            skArc(sketch, "E284", {"start": v(-18.81, -137.5) * mm, "mid": v(-18.6, -140.93) * mm, "end": v(-18.15, -144.33) * mm});
            skArc(sketch, "E285", {"start": v(-18.15, -144.33) * mm, "mid": v(-17.2, -149.77) * mm, "end": v(-16.15, -155.19) * mm});
            skArc(sketch, "E286", {"start": v(-16.15, -155.19) * mm, "mid": v(-15.31, -159.57) * mm, "end": v(-14.58, -163.98) * mm});
            skArc(sketch, "E287", {"start": v(-14.58, -163.98) * mm, "mid": v(-14.12, -167.49) * mm, "end": v(-13.82, -171.02) * mm});
            skArc(sketch, "E288", {"start": v(-13.82, -171.02) * mm, "mid": v(-13.6, -175.56) * mm, "end": v(-13.5, -180.1) * mm});
            skArc(sketch, "E289", {"start": v(-13.5, -180.1) * mm, "mid": v(-13.43, -189.6) * mm, "end": v(-13.4, -199.1) * mm});
            skArc(sketch, "E290", {"start": v(-13.4, -199.1) * mm, "mid": v(-13.37, -206.13) * mm, "end": v(-13.32, -213.17) * mm});
            skArc(sketch, "E291", {"start": v(-13.32, -213.17) * mm, "mid": v(-13.24, -217.98) * mm, "end": v(-13.1, -222.78) * mm});
            skArc(sketch, "E292", {"start": v(-13.1, -222.78) * mm, "mid": v(-12.95, -226.25) * mm, "end": v(-12.77, -229.7) * mm});
            skArc(sketch, "E293", {"start": v(-12.77, -229.7) * mm, "mid": v(-12.6, -230.68) * mm, "end": v(-12.2, -231.6) * mm});
            skArc(sketch, "E294", {"start": v(-12.2, -231.6) * mm, "mid": v(-11.4, -232.81) * mm, "end": v(-10.49, -233.94) * mm});
            skArc(sketch, "E295", {"start": v(-10.49, -233.94) * mm, "mid": v(-9.39, -235.05) * mm, "end": v(-8.2, -236.07) * mm});
            skArc(sketch, "E296", {"start": v(-8.2, -236.07) * mm, "mid": v(-6.9, -237) * mm, "end": v(-5.53, -237.81) * mm});
            skArc(sketch, "E297", {"start": v(-5.53, -237.81) * mm, "mid": v(-4.14, -238.48) * mm, "end": v(-2.7, -239.02) * mm});
            skArc(sketch, "E298", {"start": v(-2.7, -239.02) * mm, "mid": v(-1.05, -239.4) * mm, "end": v(0.64, -239.5) * mm});
            skArc(sketch, "E299", {"start": v(0.64, -239.5) * mm, "mid": v(2.4, -239.33) * mm, "end": v(4.13, -238.91) * mm});
            skArc(sketch, "E300", {"start": v(4.13, -238.91) * mm, "mid": v(5.7, -238.27) * mm, "end": v(7.14, -237.4) * mm});
            skArc(sketch, "E301", {"start": v(7.14, -237.4) * mm, "mid": v(8.23, -236.44) * mm, "end": v(9.06, -235.24) * mm});
            skArc(sketch, "E302", {"start": v(9.06, -235.24) * mm, "mid": v(10.25, -232.78) * mm, "end": v(11.23, -230.24) * mm});
            skArc(sketch, "E303", {"start": v(11.23, -230.24) * mm, "mid": v(18.28, -209.56) * mm, "end": v(25.31, -188.88) * mm});
            skArc(sketch, "E304", {"start": v(25.31, -188.88) * mm, "mid": v(32.2, -168.57) * mm, "end": v(39.07, -148.26) * mm});
            skArc(sketch, "E305", {"start": v(39.07, -148.26) * mm, "mid": v(40.17, -144.7) * mm, "end": v(41.05, -141.07) * mm});
            skArc(sketch, "E306", {"start": v(41.05, -141.07) * mm, "mid": v(41.76, -136.98) * mm, "end": v(42.13, -132.84) * mm});
            skArc(sketch, "E307", {"start": v(42.13, -132.84) * mm, "mid": v(42.1, -129.09) * mm, "end": v(41.67, -125.36) * mm});
            skArc(sketch, "E308", {"start": v(41.67, -125.36) * mm, "mid": v(40.95, -122.35) * mm, "end": v(39.84, -119.46) * mm});
            skArc(sketch, "E309", {"start": v(39.84, -119.46) * mm, "mid": v(38.55, -117.5) * mm, "end": v(36.74, -116) * mm});
            skArc(sketch, "E310", {"start": v(36.74, -116) * mm, "mid": v(35.45, -115.26) * mm, "end": v(34.1, -114.62) * mm});
            skArc(sketch, "E311", {"start": v(34.1, -114.62) * mm, "mid": v(33.14, -114.32) * mm, "end": v(32.13, -114.22) * mm});
            skArc(sketch, "E312", {"start": v(32.13, -114.22) * mm, "mid": v(31.12, -114.32) * mm, "end": v(30.15, -114.64) * mm});
            skArc(sketch, "E313", {"start": v(30.15, -114.64) * mm, "mid": v(28.8, -115.28) * mm, "end": v(27.49, -116.02) * mm});
            skSolve(sketch);
        }
        {
            var Q0;
            Q0=qSketchRegion(id+"F3",true);
            var Q1;
            Q1=sQuery(id+"F3.wireOp",EDGE,"c928f899-12af-4b01-b412-b3b7da3d830f");
            var Q2;
            Q2=sQuery(id+"F3.wireOp",EDGE,"b69f99c7-a6d0-4d1b-8752-9e82ab4c99ec");
            extrude(context, id + "F4", {"entities" : qUnion([Q0]), "operationType" : NewBodyOperationType.ADD, "surfaceEntities" : qUnion([Q1, Q2]), "depth" : 350 * mm});
        }
        {
            var Q0;
            Q0=makeQuery(id+"F4.opExtrude","SWEPT_BODY",BODY,{"disambiguationData":[OSD([sQuery(id+"F3.wireOp",EDGE,"15c6da4e-992d-4824-9d20-70d2d6be9970"),sQuery(id+"F3.wireOp",EDGE,"268c69ec-46be-456f-85eb-69decc32fe39"),sQuery(id+"F3.wireOp",EDGE,"1d386307-6059-4203-bca6-0c1cec3c82e1"),sQuery(id+"F3.wireOp",EDGE,"7d7c66d2-f869-427f-806b-ad436cacd60e"),sQuery(id+"F3.wireOp",EDGE,"1db91850-860e-493f-a3af-7a0f3f1512ae"),sQuery(id+"F3.wireOp",EDGE,"2c65f23b-9f03-4f6f-ab37-de452af29e3c"),sQuery(id+"F3.wireOp",EDGE,"ba006cbc-bbd7-44d9-84cc-9cde0967c280"),sQuery(id+"F3.wireOp",EDGE,"ae950208-c781-4a25-8fcf-ffe59b9085ff"),sQuery(id+"F3.wireOp",EDGE,"3cce0944-c62d-4831-9b9d-d1a418d328b4"),sQuery(id+"F3.wireOp",EDGE,"9edc5e7d-16c0-40c4-98ad-6b91d5df0e78"),sQuery(id+"F3.wireOp",EDGE,"aa452f44-44a2-4c64-bff5-a2a639df00db"),sQuery(id+"F3.wireOp",EDGE,"16259f99-ce20-4b7b-81e1-fa0909c03eb4"),sQuery(id+"F3.wireOp",EDGE,"79895566-a943-429d-b257-d76af3645bdf"),sQuery(id+"F3.wireOp",EDGE,"a85490ef-f17e-45c8-b92b-28215162778a"),sQuery(id+"F3.wireOp",EDGE,"322f1036-a6fd-4992-ab69-5919540af7a6"),sQuery(id+"F3.wireOp",EDGE,"0a87ff38-4ab4-4140-b3c3-2d7501d9f3b1"),sQuery(id+"F3.wireOp",EDGE,"a6e7bdf2-ef3e-49d4-9b3c-e34f5a41e0c4"),sQuery(id+"F3.wireOp",EDGE,"3e588790-576f-47c1-9730-f5e27fa1e8f9"),sQuery(id+"F3.wireOp",EDGE,"ce3739ef-15fd-4754-ad9c-ccf511a9a8fb"),sQuery(id+"F3.wireOp",EDGE,"201134a3-66f3-4a3f-aa9b-76948966efc0"),sQuery(id+"F3.wireOp",EDGE,"65b511ea-0759-428d-8070-88e1f521d8ea"),sQuery(id+"F3.wireOp",EDGE,"c37cddb6-5cf8-4891-aff4-7191a72080b9"),sQuery(id+"F3.wireOp",EDGE,"52a43dbd-e952-43e1-be3d-d70e107260e6"),sQuery(id+"F3.wireOp",EDGE,"08c1271f-f5c3-4f26-be27-7f5e21217dff"),sQuery(id+"F3.wireOp",EDGE,"59a09f58-0503-4180-962a-e04db21f0da8"),sQuery(id+"F3.wireOp",EDGE,"e56a4626-e956-42c3-bb5d-cd9dae1ca801"),sQuery(id+"F3.wireOp",EDGE,"5ff5d55f-af90-49eb-8040-353101557de8"),sQuery(id+"F3.wireOp",EDGE,"0ed7430b-e164-4f56-8af9-4534524aa7c0"),sQuery(id+"F3.wireOp",EDGE,"b5610a6e-b6bb-43e3-9a8d-d3d7c5f0098b"),sQuery(id+"F3.wireOp",EDGE,"1d417af8-88ad-47c2-a4e2-6fec82bd6695"),sQuery(id+"F3.wireOp",EDGE,"778ae99a-956a-4ddb-8078-d9bc57f9fc8e"),sQuery(id+"F3.wireOp",EDGE,"5b19af09-f144-446e-9dfa-8766819c9efd"),sQuery(id+"F3.wireOp",EDGE,"028339f6-0475-4a57-af8d-550e32ad7466"),sQuery(id+"F3.wireOp",EDGE,"d5ae35b6-d210-433a-92c8-e92622696872"),sQuery(id+"F3.wireOp",EDGE,"16a2e606-2caa-4876-9ffa-8f08c4ff3a37"),sQuery(id+"F3.wireOp",EDGE,"5b90b144-be56-4de7-a9dd-c1e0336acbe3"),sQuery(id+"F3.wireOp",EDGE,"5912d126-c5fc-41e4-bfb8-b4fefc52ca72"),sQuery(id+"F3.wireOp",EDGE,"2e96ce95-bd3e-4f27-a7f8-b62cf5efe954"),sQuery(id+"F3.wireOp",EDGE,"ecb4e259-1207-4dd0-bc3c-87c6506cc3a5"),sQuery(id+"F3.wireOp",EDGE,"105fb72e-4d79-4204-af2f-b3b26f5eb8d1"),sQuery(id+"F3.wireOp",EDGE,"fa59b598-df54-48c6-bb8f-c5f7618c69d0"),sQuery(id+"F3.wireOp",EDGE,"a6beef0d-f124-47ac-b957-e6cd3057a354"),sQuery(id+"F3.wireOp",EDGE,"7c3eaf53-dcb7-43b1-ad18-80ff953eb59e"),sQuery(id+"F3.wireOp",EDGE,"281fe206-104f-408f-94b6-be79f12604c9")])]});
            var Q1;
            Q1=makeQuery(id+"F4.opExtrude","SWEPT_BODY",BODY,{"disambiguationData":[OSD([sQuery(id+"F3.wireOp",EDGE,"58f6206a-5554-41d4-8cf7-6e0b4724a469"),sQuery(id+"F3.wireOp",EDGE,"85dabe77-b6aa-43d5-a519-64383616f71e"),sQuery(id+"F3.wireOp",EDGE,"4b679fe6-9e11-497d-b8fd-14ca14e49ddd"),sQuery(id+"F3.wireOp",EDGE,"51de25f6-d59e-4805-a327-1fd7e38869c8"),sQuery(id+"F3.wireOp",EDGE,"d47977fb-70d3-4df8-bc35-66fcc0e556e0"),sQuery(id+"F3.wireOp",EDGE,"235006b0-8f14-4ca2-82f0-f96b6b8c4766"),sQuery(id+"F3.wireOp",EDGE,"0fc7acd6-1c1d-47a8-ba12-62eb658d35ca"),sQuery(id+"F3.wireOp",EDGE,"883fa5e3-ca4c-4ce6-a249-4debf538fe24"),sQuery(id+"F3.wireOp",EDGE,"1da09ed1-22d9-43a1-a655-8acff5d61309"),sQuery(id+"F3.wireOp",EDGE,"32654a82-a09a-444f-bf73-45f818f0f235"),sQuery(id+"F3.wireOp",EDGE,"a398fd80-a0a9-4724-ba0e-1a7a000baa92"),sQuery(id+"F3.wireOp",EDGE,"f39f97c8-53f5-4046-9905-b28daecd4f10"),sQuery(id+"F3.wireOp",EDGE,"2484d883-0ec2-4c7d-9023-165ebbef226c"),sQuery(id+"F3.wireOp",EDGE,"f026d96f-3d32-4113-a1c9-3545f5cdbe4a"),sQuery(id+"F3.wireOp",EDGE,"974fee18-719e-4620-aace-d3676da2011b"),sQuery(id+"F3.wireOp",EDGE,"0c5766d2-a026-45af-bffd-0d1f783d5157"),sQuery(id+"F3.wireOp",EDGE,"5da13fee-9c04-45d8-805f-c7a03dde2383"),sQuery(id+"F3.wireOp",EDGE,"dbea32a3-85bd-4957-aef2-b6fe64a02f6b"),sQuery(id+"F3.wireOp",EDGE,"fba134ea-bf40-4191-ad8f-cc6b2b040a97"),sQuery(id+"F3.wireOp",EDGE,"0c19e200-7cd5-4fcb-83ed-261bd7936bc7"),sQuery(id+"F3.wireOp",EDGE,"246b843b-ea86-44e5-9cb9-335e6677b61d"),sQuery(id+"F3.wireOp",EDGE,"c1b3c9bc-1eb4-4c9b-99c8-0cebed89395a"),sQuery(id+"F3.wireOp",EDGE,"f93eebc3-1447-4029-8362-91325193ac2b"),sQuery(id+"F3.wireOp",EDGE,"bf86b12d-53a9-4c19-abaa-b1e658933ceb"),sQuery(id+"F3.wireOp",EDGE,"89646a71-1a60-4e14-b80a-74fb601d0855"),sQuery(id+"F3.wireOp",EDGE,"7b03dcde-0a52-4f3c-80e9-110d1d805e93"),sQuery(id+"F3.wireOp",EDGE,"83e8d1f3-8820-485b-8b6d-3ecd79124883"),sQuery(id+"F3.wireOp",EDGE,"ec7b56eb-ca95-44fd-a774-e9b7f9d3f50d"),sQuery(id+"F3.wireOp",EDGE,"31861aa6-cfd1-43ce-a7c5-bacfb7e2a30f"),sQuery(id+"F3.wireOp",EDGE,"fa3de647-1dd9-4141-982b-74ae8d07851d"),sQuery(id+"F3.wireOp",EDGE,"75d7c1c5-761c-4178-bfd4-4f469045899b"),sQuery(id+"F3.wireOp",EDGE,"4b3d7518-bd5d-4ecc-b2c5-d8dd665de4f4"),sQuery(id+"F3.wireOp",EDGE,"3be2682d-01bd-4f31-9cde-9df16a01e4a9"),sQuery(id+"F3.wireOp",EDGE,"72d3c7a9-2794-46eb-9b0d-6c526cc1b9a3"),sQuery(id+"F3.wireOp",EDGE,"0137e336-6b26-4f8d-b9ad-47ce1aa9eb31"),sQuery(id+"F3.wireOp",EDGE,"96000e4a-2d86-4b9f-af7d-a1c875cc048c"),sQuery(id+"F3.wireOp",EDGE,"139c5a79-9c0f-4e15-b57f-4c09662495a3"),sQuery(id+"F3.wireOp",EDGE,"8ea04d8b-b3da-46bb-9742-d8cba6b23bda"),sQuery(id+"F3.wireOp",EDGE,"b352b580-467e-481c-88ac-6217b8462947"),sQuery(id+"F3.wireOp",EDGE,"2503a493-1722-4539-8d54-7329fc0b116a"),sQuery(id+"F3.wireOp",EDGE,"a0615e06-0a48-4c65-8818-f0f693937022"),sQuery(id+"F3.wireOp",EDGE,"08389002-1ce8-438a-b5a4-698ca33590c2"),sQuery(id+"F3.wireOp",EDGE,"1756e4aa-c30a-461e-962c-81ee35d31e55"),sQuery(id+"F3.wireOp",EDGE,"5f84c249-07ea-4efb-9be3-ca494937f772"),sQuery(id+"F3.wireOp",EDGE,"cbefd041-b54f-4587-87b6-437b2290d1fc"),sQuery(id+"F3.wireOp",EDGE,"d44f58d4-f1a7-4aec-b016-8e7f1e498aeb"),sQuery(id+"F3.wireOp",EDGE,"0a5be90b-7545-44ea-9f2d-c726a5a2121c"),sQuery(id+"F3.wireOp",EDGE,"0cfaa442-d102-4580-8ef6-489f2aa1e6b3")])]});
            var Q2;
            Q2=makeQuery(id+"F4.opExtrude","SWEPT_BODY",BODY,{"disambiguationData":[OSD([sQuery(id+"F3.wireOp",EDGE,"9cc7aec6-4d94-4577-ab6c-32f5aa316238"),sQuery(id+"F3.wireOp",EDGE,"5ab2d840-4a32-405a-8c4b-a8126e3e1bc1"),sQuery(id+"F3.wireOp",EDGE,"56de48b4-9620-4637-8196-310e2641530f"),sQuery(id+"F3.wireOp",EDGE,"55327826-e64b-4830-85f2-3f22d36f43b5"),sQuery(id+"F3.wireOp",EDGE,"0245b46f-a639-4a95-8ca3-1568736ceed2"),sQuery(id+"F3.wireOp",EDGE,"9bd8a002-6ca7-4c84-8984-a620eefad103"),sQuery(id+"F3.wireOp",EDGE,"d4736c5e-da0b-46a0-ba9d-17ae07bb2b66"),sQuery(id+"F3.wireOp",EDGE,"125695b8-77e6-4e99-8f78-5f8fae1a0c71"),sQuery(id+"F3.wireOp",EDGE,"c9f25b10-a495-4684-8f25-8f255fabab6e"),sQuery(id+"F3.wireOp",EDGE,"0dbee67a-2ab6-4abb-ae16-0fe64d623848"),sQuery(id+"F3.wireOp",EDGE,"92c08d8e-ed2e-41a3-9c1a-b5ddaf8a0bf1"),sQuery(id+"F3.wireOp",EDGE,"00fabb15-0c1e-492e-85c1-17390e5b12bc"),sQuery(id+"F3.wireOp",EDGE,"065a9352-dddb-4e3f-b02a-444c867b75fe"),sQuery(id+"F3.wireOp",EDGE,"ef206bb6-e4f2-4189-9fc7-a7823c329ad6"),sQuery(id+"F3.wireOp",EDGE,"7199cbbe-c9bf-4cb9-b928-2ff8a84eb09e"),sQuery(id+"F3.wireOp",EDGE,"17bf9ed1-b881-4f74-816d-3511b6b328c7"),sQuery(id+"F3.wireOp",EDGE,"e5b615d0-4193-495d-b285-bd69ae30f000"),sQuery(id+"F3.wireOp",EDGE,"cfeaf62f-6be1-426b-9732-01e1a667be7e"),sQuery(id+"F3.wireOp",EDGE,"ac56344b-5ee6-4fa5-8e47-65b2a4ea3a01"),sQuery(id+"F3.wireOp",EDGE,"45b5fa53-15fd-43a0-91b0-943cc3286fc9")])]});
            var Q3;
            Q3=makeQuery(id+"F4.opExtrude","SWEPT_BODY",BODY,{"disambiguationData":[OSD([sQuery(id+"F3.wireOp",EDGE,"7bdfe37d-9957-4663-8239-5490fd3220d9"),sQuery(id+"F3.wireOp",EDGE,"6a91314f-c002-4565-bbf8-bb9f29165fb8"),sQuery(id+"F3.wireOp",EDGE,"b69f99c7-a6d0-4d1b-8752-9e82ab4c99ec"),sQuery(id+"F3.wireOp",EDGE,"c928f899-12af-4b01-b412-b3b7da3d830f"),sQuery(id+"F3.wireOp",EDGE,"ffa58721-cdd5-406d-be26-d96f7a050df4"),sQuery(id+"F3.wireOp",EDGE,"02fc7fb8-293b-44ff-ab78-63506d0aedb9"),sQuery(id+"F3.wireOp",EDGE,"147fb6cb-2565-4fb5-9280-6afbf9eef36b"),sQuery(id+"F3.wireOp",EDGE,"2cee3704-4124-415a-b391-31af1cf305d7"),sQuery(id+"F3.wireOp",EDGE,"32b2fb71-03c8-4978-9d95-2b5aaf044d0d"),sQuery(id+"F3.wireOp",EDGE,"e5d05796-7d6c-4350-8a4e-d55f5ade2f77"),sQuery(id+"F3.wireOp",EDGE,"77b1164c-8dd4-4680-b616-ac151a422eb2"),sQuery(id+"F3.wireOp",EDGE,"ec0798b8-0fbb-49ea-9766-39d2ee0936b0"),sQuery(id+"F3.wireOp",EDGE,"c4af6478-2a03-47a6-862f-c0c71886b8a3"),sQuery(id+"F3.wireOp",EDGE,"1912a38f-fa28-45c6-ab33-84cac2787056"),sQuery(id+"F3.wireOp",EDGE,"5d79fa95-f66d-4d2b-923b-4d54735f1fbd"),sQuery(id+"F3.wireOp",EDGE,"2db7aef4-a710-4bcf-9c1c-a8a87719953d"),sQuery(id+"F3.wireOp",EDGE,"183449de-345c-4115-9bca-43a403e62dbd"),sQuery(id+"F3.wireOp",EDGE,"e3ac8c9b-cab5-44b0-ad81-0e2b680c384a"),sQuery(id+"F3.wireOp",EDGE,"92e85db6-f458-41f6-a9a1-1e1a1a7e7809"),sQuery(id+"F3.wireOp",EDGE,"f0dbb46f-43a9-447b-9c75-8dfc9b95470d"),sQuery(id+"F3.wireOp",EDGE,"4b73f5f6-f769-4414-bdba-7d253e58fff4"),sQuery(id+"F3.wireOp",EDGE,"a88669dc-35b3-46bb-964f-c9bf6c4ab898"),sQuery(id+"F3.wireOp",EDGE,"2c559bae-f38f-4377-91e6-3c9de70acf11"),sQuery(id+"F3.wireOp",EDGE,"c1caf99b-adaa-42fe-a319-8cbcd819cf89"),sQuery(id+"F3.wireOp",EDGE,"54b04dd4-0ec4-4956-b19c-1141095738e3"),sQuery(id+"F3.wireOp",EDGE,"098f7a84-b7b8-4879-b21a-5c38879e4110"),sQuery(id+"F3.wireOp",EDGE,"b406a8e6-a226-4f3d-ac30-e4d06e4dac62"),sQuery(id+"F3.wireOp",EDGE,"36f95d1d-68ce-4231-ad71-3960c85e5915"),sQuery(id+"F3.wireOp",EDGE,"dc12cad8-2eed-454e-aa74-30099b1c9064"),sQuery(id+"F3.wireOp",EDGE,"4c78a4fd-cd81-43d6-85d6-6e4d3fbc1e98"),sQuery(id+"F3.wireOp",EDGE,"ee9e30de-787b-4e8f-b425-43a8e9289f81"),sQuery(id+"F3.wireOp",EDGE,"2518a3a4-c96b-4463-8704-0b71c65c60d2"),sQuery(id+"F3.wireOp",EDGE,"c9129a67-398c-4e37-92cb-2d54ff2e2e82"),sQuery(id+"F3.wireOp",EDGE,"d429d547-9f5b-42c6-bcca-effad2fa908f"),sQuery(id+"F3.wireOp",EDGE,"99d16e94-b2b3-43d5-9c7b-7bd463994dcb"),sQuery(id+"F3.wireOp",EDGE,"32993909-9a70-47ee-9097-89fff220f839"),sQuery(id+"F3.wireOp",EDGE,"6eabbeed-9496-4825-b168-63782a34f495"),sQuery(id+"F3.wireOp",EDGE,"f74987e3-8e60-4a5b-857f-839ae8aaf0cf"),sQuery(id+"F3.wireOp",EDGE,"1c218c86-035d-4441-93c0-9621d3297c3a"),sQuery(id+"F3.wireOp",EDGE,"0133f513-4b11-4cc4-b075-4625e9591e41"),sQuery(id+"F3.wireOp",EDGE,"fe921ad4-a8f5-4772-9aeb-350aca2e8948"),sQuery(id+"F3.wireOp",EDGE,"bfde0a4f-3cec-4f8e-8a23-dd1441b34c2b"),sQuery(id+"F3.wireOp",EDGE,"b41521ff-c5df-4b64-83ed-5e7635cf4438"),sQuery(id+"F3.wireOp",EDGE,"ed692599-6bbb-4379-8e89-ea326a0a0f87"),sQuery(id+"F3.wireOp",EDGE,"a98451c0-d76c-436e-99f9-a3fe9c8430a4"),sQuery(id+"F3.wireOp",EDGE,"561965b2-3050-4f49-9305-d98a2b852bbe"),sQuery(id+"F3.wireOp",EDGE,"e13dfa59-48e6-4b4e-94b9-1fc5254b0f2e"),sQuery(id+"F3.wireOp",EDGE,"0354e106-253a-4bfa-b5b7-b09cd0f2f6c0"),sQuery(id+"F3.wireOp",EDGE,"8df1dcc8-d00a-4777-85fd-8af8e9830bd1"),sQuery(id+"F3.wireOp",EDGE,"26ce3762-0d1a-4b81-9a23-debcfc24da1c"),sQuery(id+"F3.wireOp",EDGE,"3e900f8f-3ffb-4e32-b536-61fea2f3e30a"),sQuery(id+"F3.wireOp",EDGE,"4a1b5445-5559-461f-b6f1-b4cd9b95ea10")])]});
            var Q4;
            Q4=makeQuery(id+"F1.opRevolve","SWEPT_BODY",BODY,{"disambiguationData":[OSD([sQuery(id+"F0.wireOp",EDGE,"E0"),sQuery(id+"F0.wireOp",EDGE,"E1")])]});
            var Q5;
            Q5=qCreatedBy(makeId("Origin.pointOp"),VERTEX);
            transform(context, id + "F5", {"entities" : qUnion([Q0, Q1, Q2, Q3, Q4]), "transformType" : TransformType.SCALE_UNIFORMLY, "scale" : 0.03, "scalePoint" : qUnion([Q5]), "makeCopy" : false});
        }
        {
            var Q0;
            Q0=qCreatedBy(makeId("Top.planeOp"),FACE);
            var sketch = newSketch(context, id + "F6", { "sketchPlane" : qUnion([Q0])});
            skLineSegment(sketch, "E314", {"start": v(0, 15) * mm, "end": v(0, -15) * mm});
            skArc(sketch, "E315", {"start": v(0, 15) * mm, "mid": v(-15, 0) * mm, "end": v(0, -15) * mm});
            skArc(sketch, "E316", {"start": v(0, 10.25) * mm, "mid": v(-10.25, 0) * mm, "end": v(0, -10.25) * mm});
            skArc(sketch, "E317", {"start": v(0, 7) * mm, "mid": v(-7, 0) * mm, "end": v(0, -7) * mm});
            skSolve(sketch);
        }
        {
            var Q0;
            {var subQ0=sQuery(id+"F6.wireOp",EDGE,"E315");Q0=makeQuery(id+"F6.imprint","IMPRINT",FACE,{"disambiguationData":[TD([[makeQuery(id+"F6.imprint","IMPRINT",EDGE,{"derivedFrom":subQ0}),1.0]])]});}
            var Q1;
            {var subQ0=sQuery(id+"F6.wireOp",EDGE,"E317");Q1=makeQuery(id+"F6.imprint","IMPRINT",FACE,{"disambiguationData":[TD([[makeQuery(id+"F6.imprint","IMPRINT",EDGE,{"derivedFrom":subQ0}),1.0]])]});}
            var Q2;
            Q2=sQuery(id+"F6.wireOp",EDGE,"E314");
            revolve(context, id + "F7", {"operationType" : NewBodyOperationType.REMOVE, "entities" : qUnion([Q0, Q1]), "axis" : qUnion([Q2]), "revolveType" : RevolveType.FULL});
        }
        {
            var Q0;
            Q0=makeQuery(id+"F1.opRevolve","SWEPT_BODY",BODY,{"disambiguationData":[OSD([sQuery(id+"F0.wireOp",EDGE,"E0"),sQuery(id+"F0.wireOp",EDGE,"E1")])]});
            var Q1;
            Q1=sQuery(id+"F0.wireOp",VERTEX,"E1.center");
            transform(context, id + "F8", {"entities" : qUnion([Q0]), "transformType" : TransformType.SCALE_UNIFORMLY, "scale" : 1.4, "scalePoint" : qUnion([Q1]), "makeCopy" : false});
        }
        {
            var Q0;
            Q0=qCreatedBy(makeId("Front.planeOp"),FACE);
            var sketch = newSketch(context, id + "F9", { "sketchPlane" : qUnion([Q0])});
            skCircle(sketch, "E318", {"center": v(0, -5.12) * mm, "radius": 2 * mm});
            skSolve(sketch);
        }
        {
            var Q0;
            Q0=qSketchRegion(id+"F9",true);
            extrude(context, id + "F10", {"entities" : qUnion([Q0]), "operationType" : NewBodyOperationType.REMOVE, "oppositeDirection" : true, "depth" : 25 * mm});
        }
    });
